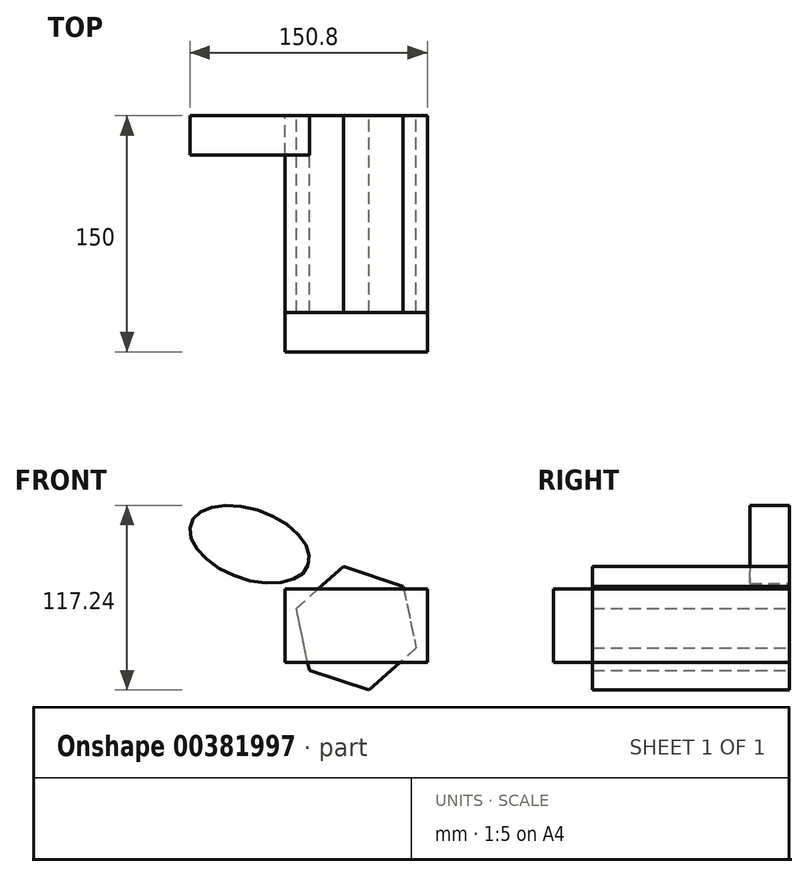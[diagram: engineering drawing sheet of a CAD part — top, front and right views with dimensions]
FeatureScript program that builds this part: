
annotation { "Feature Type Name" : "Feature", "Feature Type Description" : "" }
export const myFeature = defineFeature(function(context is Context, id is Id, definition is map)
    precondition{}
    {
        {
            var Q0;
            Q0=qCreatedBy(makeId("Front.planeOp"),FACE);
            var sketch = newSketch(context, id + "F0", { "sketchPlane" : qUnion([Q0])});
            skCircle(sketch, "E0.cCircle", {"center": v(0, 0) * mm, "radius": 34.64 * mm, "construction": true});
            skLineSegment(sketch, "E0.0", {"start": v(-38, 12.46) * mm, "end": v(-8.21, 39.15) * mm});
            skLineSegment(sketch, "E0.1", {"start": v(-8.21, 39.15) * mm, "end": v(29.8, 26.69) * mm});
            skLineSegment(sketch, "E0.2", {"start": v(29.8, 26.69) * mm, "end": v(38, -12.46) * mm});
            skLineSegment(sketch, "E0.3", {"start": v(38, -12.46) * mm, "end": v(8.21, -39.15) * mm});
            skLineSegment(sketch, "E0.4", {"start": v(8.21, -39.15) * mm, "end": v(-29.8, -26.69) * mm});
            skLineSegment(sketch, "E0.5", {"start": v(-29.8, -26.69) * mm, "end": v(-38, 12.46) * mm});
            skPoint(sketch, "E0.0.midPoint", {"position": v(-23.11, 25.8) * mm});
            skSolve(sketch);
        }
        {
            var Q0;
            Q0=qCreatedBy(makeId("Front.planeOp"),FACE);
            var sketch = newSketch(context, id + "F1", { "sketchPlane" : qUnion([Q0])});
            skLineSegment(sketch, "E1.bottom", {"start": v(45.18, 24.86) * mm, "end": v(-45.18, 24.86) * mm});
            skLineSegment(sketch, "E1.top", {"start": v(45.18, -21.6) * mm, "end": v(-45.18, -21.6) * mm});
            skLineSegment(sketch, "E1.left", {"start": v(45.18, 24.86) * mm, "end": v(45.18, -21.6) * mm});
            skLineSegment(sketch, "E1.right", {"start": v(-45.18, 24.86) * mm, "end": v(-45.18, -21.6) * mm});
            skPoint(sketch, "E1.middle", {"position": v(0, 1.63) * mm});
            skSolve(sketch);
        }
        {
            var Q0;
            Q0 = qSketchRegion(id + "F0", true);
            var Q1;
            Q1=makeQuery(id+"F1.imprint","IMPRINT",FACE,{"disambiguationData":[TD([[makeQuery(id+"F1.imprint","IMPRINT",EDGE,{"derivedFrom":sQuery(id+"F1.wireOp",EDGE,"E1.bottom")}),1.0]])]});
            extrude(context, id + "F2", {"entities" : qUnion([Q0, Q1]), "depth" : 125 * mm});
        }
        {
            var Q0;
            Q0=makeQuery(id+"F2.opExtrude","CAP_FACE",FACE,{"disambiguationData":[OSD([sQuery(id+"F1.wireOp",EDGE,"E1.bottom"),sQuery(id+"F1.wireOp",EDGE,"E1.top"),sQuery(id+"F1.wireOp",EDGE,"E1.left"),sQuery(id+"F1.wireOp",EDGE,"E1.right")])],"isStart":false});
            extrude(context, id + "F3", {"entities" : qUnion([Q0]), "depth" : 25 * mm});
        }
        {
            var Q0;
            Q0=qCreatedBy(makeId("Front.planeOp"),FACE);
            var sketch = newSketch(context, id + "F4", { "sketchPlane" : qUnion([Q0])});
            skEllipse(sketch, "E2", {"center": v(-67.68, 53.35) * mm, "majorRadius": 39.49 * mm, "minorRadius": 22.19 * mm, "majorAxis": v(0.94, -0.34)});
            skSolve(sketch);
        }
        {
            var Q0;
            Q0 = qSketchRegion(id + "F4", true);
            extrude(context, id + "F5", {"entities" : qUnion([Q0]), "depth" : 25 * mm});
        }
    });
